# Revit family: xxxSolid_Interceptor-Hair_Lint-Jay_R_Smith-87X0T_Series
name_source: partatom
category: Specialty Equipment
units: mm (PartAtom-declared; Revit-internal decimal feet)

## family parameters
Cut with Voids When Loaded = No
Host = Face
OmniClass Number = 23.45.30.00
OmniClass Title = Washing and Waste Disposal Equipment
Part Type = Normal
Room Calculation Point = No
Round Connector Dimension = Use Diameter
Shared = Yes

## types (2) — shared parameters
-CI Duco Cast Iron = No
-CP Chrome Plated Cast Iron = No
-PB Polished Bronze = No
0125 Pipe Size = Yes
0150 Pipe Size = No
Assembly Code = D2090300
Connection Inlet Description = 1 1/4-inch Waste Inlet Connection
Connection Outlet Description = 1 1/4-inch Waste Outlet Connection
Default Elevation = 0"
Description = Solids Interceptors Suspended Type Hair and Lint Interceptors
Diameter 1 = 1 1/2"
Finish = Bronze-JayRSmith-Chrome Plated
Height = 7 1/4"
Inlet Diameter Connection = 1 1/4"
Installation Type = Wall Mounted
Manufacturer = Jay R. Smith
Material = Bronze-JayRSmith-Chrome Plated
Others = Metal-JayRSmith-Stainless Steel
Outer Rim = 3/4"
Outlet Diameter Connection = 1 1/4"
Price = Prices may vary. Please consult Manufacturer Representative for most up-to-date price list.
Product Documentation Link = https://www.jrsmith.com
Product Page URL = https://www.jrsmith.com
URL = https://www.jrsmith.com
Warranty Documentation Link = https://www.jrsmith.com
Width = 3 1/2"

## per-type parameters (varying)
| type | 8750T | 8760T | Outlet Elbow Height |
| 8750T | Yes | No | 5 3/4" |
| 8760T | No | Yes | 9 1/4" |

note: column(s) folded — value = type name in every type: Model

## geometry (parser evidence)
native form markers: Sweep x2
no freeform markers — native parametric forms only
